# Revit family: Towel_Ring-Wall_Mounted-American_Standard-CR_Series-8336.190
name_source: partatom
category: Specialty Equipment
revit_build: Autodesk Revit 2014 (Build: 20130308_1515(x64)
units: mm (PartAtom-declared; Revit-internal decimal feet)

## types (1)
- 9336.190
    Assembly Code = C1030220
    Default Elevation = 40"
    Description = CR Series Towel Ring with concealed mounting.
    Height = 8 1/8"
    Installation Type = Wall Mounted
    Length = 3"
    Manufacturer = American Standard
    Material = Metal-American Standard-002-Polished Chrome
    Model = 9336.190
    Price = Prices may vary. Please consult Manufacturer Representative for most up-to-date price list.
    Product Documentation Link = https://www.americanstandard-us.com
    Product Page URL = https://www.americanstandard-us.com
    Revised Date = 11/22/2016
    URL = http://www.americanstandard-us.com
    Width = 7 1/8"

## geometry (parser evidence)
native form markers: Sweep x3
no freeform markers — native parametric forms only
